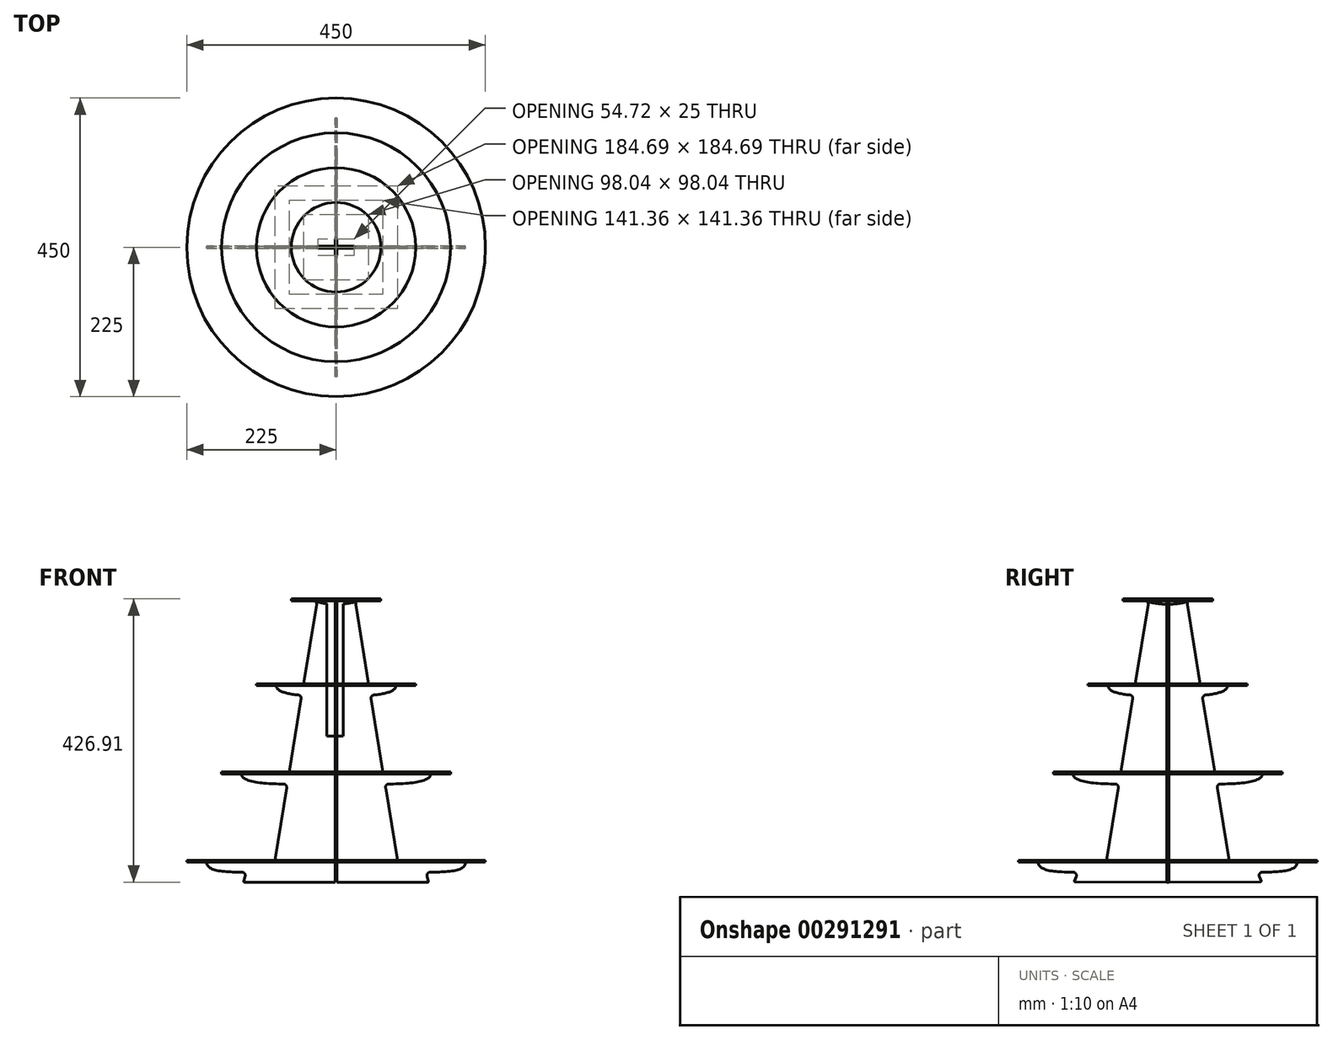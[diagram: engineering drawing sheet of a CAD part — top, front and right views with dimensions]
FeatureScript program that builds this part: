
annotation { "Feature Type Name" : "Feature", "Feature Type Description" : "" }
export const myFeature = defineFeature(function(context is Context, id is Id, definition is map)
    precondition{}
    {
        {
            var Q0;
            Q0=qCreatedBy(makeId("Front.planeOp"),FACE);
            var sketch = newSketch(context, id + "F0", { "sketchPlane" : qUnion([Q0])});
            skLineSegment(sketch, "E0.bottom", {"start": v(-225, 33) * mm, "end": v(225, 33) * mm, "construction": true});
            skLineSegment(sketch, "E0.top", {"start": v(-225, 30) * mm, "end": v(225, 30) * mm, "construction": true});
            skLineSegment(sketch, "E0.left", {"start": v(-225, 33) * mm, "end": v(-225, 30) * mm, "construction": true});
            skLineSegment(sketch, "E0.right", {"start": v(225, 33) * mm, "end": v(225, 30) * mm, "construction": true});
            skLineSegment(sketch, "E1.bottom", {"start": v(-172.5, 166) * mm, "end": v(172.5, 166) * mm, "construction": true});
            skLineSegment(sketch, "E1.top", {"start": v(-172.5, 163) * mm, "end": v(172.5, 163) * mm, "construction": true});
            skLineSegment(sketch, "E1.left", {"start": v(-172.5, 166) * mm, "end": v(-172.5, 163) * mm, "construction": true});
            skLineSegment(sketch, "E1.right", {"start": v(172.5, 166) * mm, "end": v(172.5, 163) * mm, "construction": true});
            skLineSegment(sketch, "E2.bottom", {"start": v(-120, 299) * mm, "end": v(120, 299) * mm, "construction": true});
            skLineSegment(sketch, "E2.top", {"start": v(-120, 296) * mm, "end": v(120, 296) * mm, "construction": true});
            skLineSegment(sketch, "E2.left", {"start": v(-120, 299) * mm, "end": v(-120, 296) * mm, "construction": true});
            skLineSegment(sketch, "E2.right", {"start": v(120, 299) * mm, "end": v(120, 296) * mm, "construction": true});
            skLineSegment(sketch, "E3.bottom", {"start": v(-67.5, 432) * mm, "end": v(67.5, 432) * mm, "construction": true});
            skLineSegment(sketch, "E3.top", {"start": v(-67.5, 429) * mm, "end": v(67.5, 429) * mm, "construction": true});
            skLineSegment(sketch, "E3.left", {"start": v(-67.5, 432) * mm, "end": v(-67.5, 429) * mm, "construction": true});
            skLineSegment(sketch, "E3.right", {"start": v(67.5, 432) * mm, "end": v(67.5, 429) * mm, "construction": true});
            skLineSegment(sketch, "E4", {"start": v(0, 0) * mm, "end": v(0, 600) * mm, "construction": true});
            skPoint(sketch, "E5", {"position": v(0, 30) * mm});
            skPoint(sketch, "E6", {"position": v(0, 163) * mm});
            skLineSegment(sketch, "E7", {"start": v(-225, 30) * mm, "end": v(0, 600) * mm, "construction": true});
            skPoint(sketch, "E8", {"position": v(0, 429) * mm});
            skPoint(sketch, "E9", {"position": v(0, 296) * mm});
            skFitSpline(sketch, "E10", {"points": [v(-195, 30) * mm, v(-135, 15) * mm], "startDerivative": vector(0, -45) * mm, "endDerivative": vector(85.44, 0) * mm});
            skFitSpline(sketch, "E11", {"points": [v(-142.5, 163) * mm, v(-82.5, 148) * mm], "startDerivative": vector(0, -35.84) * mm, "endDerivative": vector(85.44, 0) * mm});
            skLineSegment(sketch, "E12", {"start": v(-82.5, 148) * mm, "end": v(-79.5, 148) * mm});
            skFitSpline(sketch, "E13", {"points": [v(-90, 296) * mm, v(-30, 281) * mm], "startDerivative": vector(0, -35.84) * mm, "endDerivative": vector(85.44, 0) * mm});
            skLineSegment(sketch, "E14", {"start": v(-30, 281) * mm, "end": v(-3.68, 281) * mm});
            skFitSpline(sketch, "E15", {"points": [v(-37.5, 429) * mm, v(23.68, 417.72) * mm], "startDerivative": vector(0, -35.84) * mm, "endDerivative": vector(-10.64, 0) * mm});
            skLineSegment(sketch, "E16", {"start": v(-19.74, 478.8) * mm, "end": v(-27.36, 432) * mm});
            skLineSegment(sketch, "E17.trimOffspring", {"start": v(-74.56, 142.2) * mm, "end": v(-92.34, 33) * mm});
            skLineSegment(sketch, "E18.trimOffspring", {"start": v(-52.71, 276.35) * mm, "end": v(-70.68, 166) * mm});
            skLineSegment(sketch, "E19.trimOffspring", {"start": v(-29.56, 418.53) * mm, "end": v(-49.02, 299) * mm});
            skLineSegment(sketch, "E20", {"start": v(-92.34, 33) * mm, "end": v(-92.34, 30) * mm});
            skLineSegment(sketch, "E21", {"start": v(-92.34, 30) * mm, "end": v(-195, 30) * mm});
            skLineSegment(sketch, "E22", {"start": v(-70.68, 166) * mm, "end": v(-70.68, 163) * mm});
            skLineSegment(sketch, "E23", {"start": v(-70.68, 163) * mm, "end": v(-142.5, 163) * mm});
            skLineSegment(sketch, "E24", {"start": v(-49.02, 299) * mm, "end": v(-49.02, 296) * mm});
            skLineSegment(sketch, "E25", {"start": v(-49.02, 296) * mm, "end": v(-90, 296) * mm});
            skLineSegment(sketch, "E26", {"start": v(-27.36, 432) * mm, "end": v(-27.36, 429) * mm});
            skLineSegment(sketch, "E27", {"start": v(-27.36, 429) * mm, "end": v(-37.5, 429) * mm});
            skLineSegment(sketch, "E28", {"start": v(-137.04, 8.5) * mm, "end": v(-139.31, 1.3) * mm});
            skLineSegment(sketch, "E29", {"start": v(-138.36, 0) * mm, "end": v(0, 0) * mm});
            skArc(sketch, "E30.filletArc", {"start": v(-137.04, 8.5) * mm, "mid": v(-137.78, 12.96) * mm, "end": v(-141.8, 15) * mm});
            skPoint(sketch, "E31.visualSharp", {"position": v(-139.72, 0) * mm});
            skArc(sketch, "E31.filletArc", {"start": v(-139.31, 1.3) * mm, "mid": v(-139.16, 0.4) * mm, "end": v(-138.36, 0) * mm});
            skPoint(sketch, "E32.visualSharp", {"position": v(-73.61, 148) * mm});
            skArc(sketch, "E32.filletArc", {"start": v(-74.56, 142.2) * mm, "mid": v(-75.68, 146.24) * mm, "end": v(-79.5, 148) * mm});
            skPoint(sketch, "E33.visualSharp", {"position": v(-51.84, 281.7) * mm});
            skArc(sketch, "E33.filletArc", {"start": v(-52.71, 276.35) * mm, "mid": v(-53.69, 280.2) * mm, "end": v(-57.17, 282.13) * mm});
            skPoint(sketch, "E34.visualSharp", {"position": v(-28.89, 422.61) * mm});
            skArc(sketch, "E34.filletArc", {"start": v(-29.56, 418.53) * mm, "mid": v(-30.1, 421.72) * mm, "end": v(-32.48, 423.9) * mm});
            skLineSegment(sketch, "E35.MirrorCS", {"start": v(19.74, 478.8) * mm, "end": v(27.36, 432) * mm});
            skLineSegment(sketch, "E36.MirrorCS", {"start": v(27.36, 432) * mm, "end": v(27.36, 429) * mm});
            skLineSegment(sketch, "E37.MirrorCS", {"start": v(27.36, 429) * mm, "end": v(37.5, 429) * mm});
            skLineSegment(sketch, "E38.MirrorCS", {"start": v(67.5, 429) * mm, "end": v(-67.5, 429) * mm, "construction": true});
            skFitSpline(sketch, "E39.MirrorCS", {"points": [v(37.5, 429) * mm, v(-23.68, 417.72) * mm], "startDerivative": vector(0, -35.84) * mm, "endDerivative": vector(10.64, 0) * mm});
            skArc(sketch, "E40.MirrorCS", {"start": v(29.56, 418.53) * mm, "mid": v(30.1, 421.72) * mm, "end": v(32.48, 423.9) * mm});
            skLineSegment(sketch, "E41.MirrorCS", {"start": v(29.56, 418.53) * mm, "end": v(49.02, 299) * mm});
            skLineSegment(sketch, "E42.MirrorCS", {"start": v(49.02, 299) * mm, "end": v(49.02, 296) * mm});
            skLineSegment(sketch, "E43.MirrorCS", {"start": v(49.02, 296) * mm, "end": v(90, 296) * mm});
            skLineSegment(sketch, "E44.MirrorCS", {"start": v(120, 296) * mm, "end": v(-120, 296) * mm, "construction": true});
            skFitSpline(sketch, "E45.MirrorCS", {"points": [v(90, 296) * mm, v(30, 281) * mm], "startDerivative": vector(0, -35.84) * mm, "endDerivative": vector(-85.44, 0) * mm});
            skArc(sketch, "E46.MirrorCS", {"start": v(52.71, 276.35) * mm, "mid": v(53.69, 280.2) * mm, "end": v(57.17, 282.13) * mm});
            skLineSegment(sketch, "E47.MirrorCS", {"start": v(52.71, 276.35) * mm, "end": v(70.68, 166) * mm});
            skLineSegment(sketch, "E48.MirrorCS", {"start": v(70.68, 166) * mm, "end": v(70.68, 163) * mm});
            skLineSegment(sketch, "E49.MirrorCS", {"start": v(70.68, 163) * mm, "end": v(142.5, 163) * mm});
            skLineSegment(sketch, "E50.MirrorCS", {"start": v(172.5, 163) * mm, "end": v(-172.5, 163) * mm, "construction": true});
            skFitSpline(sketch, "E51.MirrorCS", {"points": [v(142.5, 163) * mm, v(82.5, 148) * mm], "startDerivative": vector(0, -35.84) * mm, "endDerivative": vector(-85.44, 0) * mm});
            skLineSegment(sketch, "E52.MirrorCS", {"start": v(74.56, 142.2) * mm, "end": v(92.34, 33) * mm});
            skLineSegment(sketch, "E53.MirrorCS", {"start": v(82.5, 148) * mm, "end": v(79.5, 148) * mm});
            skArc(sketch, "E54.MirrorCS", {"start": v(74.56, 142.2) * mm, "mid": v(75.68, 146.24) * mm, "end": v(79.5, 148) * mm});
            skPoint(sketch, "E55.MirrorP", {"position": v(73.61, 148) * mm});
            skLineSegment(sketch, "E56.MirrorCS", {"start": v(92.34, 30) * mm, "end": v(195, 30) * mm});
            skLineSegment(sketch, "E57.MirrorCS", {"start": v(225, 30) * mm, "end": v(-225, 30) * mm, "construction": true});
            skLineSegment(sketch, "E58.MirrorCS", {"start": v(92.34, 33) * mm, "end": v(92.34, 30) * mm});
            skFitSpline(sketch, "E59.MirrorCS", {"points": [v(195, 30) * mm, v(135, 15) * mm], "startDerivative": vector(0, -45) * mm, "endDerivative": vector(-85.44, 0) * mm});
            skArc(sketch, "E60.MirrorCS", {"start": v(137.04, 8.5) * mm, "mid": v(137.78, 12.96) * mm, "end": v(141.8, 15) * mm});
            skLineSegment(sketch, "E61.MirrorCS", {"start": v(137.04, 8.5) * mm, "end": v(139.31, 1.3) * mm});
            skArc(sketch, "E62.MirrorCS", {"start": v(139.31, 1.3) * mm, "mid": v(139.16, 0.4) * mm, "end": v(138.36, 0) * mm});
            skLineSegment(sketch, "E63.MirrorCS", {"start": v(138.36, 0) * mm, "end": v(0, 0) * mm});
            skPoint(sketch, "E64.visualSharp", {"position": v(0, 600) * mm});
            skPoint(sketch, "E65", {"position": v(0, 475.58) * mm});
            skArc(sketch, "E66.filletArc", {"start": v(19.74, 478.8) * mm, "mid": v(0, 495.58) * mm, "end": v(-19.74, 478.8) * mm});
            skCircle(sketch, "E67", {"center": v(0, 475.58) * mm, "radius": 10 * mm});
            skPoint(sketch, "E68", {"position": v(0, 495.58) * mm});
            skSolve(sketch);
        }
        {
            var Q0;
            Q0=makeQuery(id+"F0.imprint","IMPRINT",FACE,{"disambiguationData":[TD([[makeQuery(id+"F0.imprint","IMPRINT",EDGE,{"derivedFrom":sQuery(id+"F0.wireOp",EDGE,"E10")}),1.0]])]});
            extrude(context, id + "F1", {"entities" : qUnion([Q0]), "endBound" : BoundingType.SYMMETRIC, "depth" : 3 * mm});
        }
        {
            var Q0;
            Q0=makeQuery(id+"F1.opExtrude","CAP_FACE",FACE,{"disambiguationData":[OSD([sQuery(id+"F0.wireOp",EDGE,"E10"),sQuery(id+"F0.wireOp",EDGE,"E11"),sQuery(id+"F0.wireOp",EDGE,"E12"),sQuery(id+"F0.wireOp",EDGE,"E13"),sQuery(id+"F0.wireOp",EDGE,"E15"),sQuery(id+"F0.wireOp",EDGE,"E16"),sQuery(id+"F0.wireOp",EDGE,"E17.trimOffspring"),sQuery(id+"F0.wireOp",EDGE,"E18.trimOffspring"),sQuery(id+"F0.wireOp",EDGE,"E19.trimOffspring"),sQuery(id+"F0.wireOp",EDGE,"E20"),sQuery(id+"F0.wireOp",EDGE,"E21"),sQuery(id+"F0.wireOp",EDGE,"E22"),sQuery(id+"F0.wireOp",EDGE,"E23"),sQuery(id+"F0.wireOp",EDGE,"E24"),sQuery(id+"F0.wireOp",EDGE,"E25"),sQuery(id+"F0.wireOp",EDGE,"E26"),sQuery(id+"F0.wireOp",EDGE,"E27"),sQuery(id+"F0.wireOp",EDGE,"E28"),sQuery(id+"F0.wireOp",EDGE,"E29"),sQuery(id+"F0.wireOp",EDGE,"E30.filletArc"),sQuery(id+"F0.wireOp",EDGE,"E31.filletArc"),sQuery(id+"F0.wireOp",EDGE,"E32.filletArc"),sQuery(id+"F0.wireOp",EDGE,"E33.filletArc"),sQuery(id+"F0.wireOp",EDGE,"E34.filletArc"),sQuery(id+"F0.wireOp",EDGE,"E35.MirrorCS"),sQuery(id+"F0.wireOp",EDGE,"E36.MirrorCS"),sQuery(id+"F0.wireOp",EDGE,"E37.MirrorCS"),sQuery(id+"F0.wireOp",EDGE,"E39.MirrorCS"),sQuery(id+"F0.wireOp",EDGE,"E40.MirrorCS"),sQuery(id+"F0.wireOp",EDGE,"E41.MirrorCS"),sQuery(id+"F0.wireOp",EDGE,"E42.MirrorCS"),sQuery(id+"F0.wireOp",EDGE,"E43.MirrorCS"),sQuery(id+"F0.wireOp",EDGE,"E45.MirrorCS"),sQuery(id+"F0.wireOp",EDGE,"E46.MirrorCS"),sQuery(id+"F0.wireOp",EDGE,"E47.MirrorCS"),sQuery(id+"F0.wireOp",EDGE,"E48.MirrorCS"),sQuery(id+"F0.wireOp",EDGE,"E49.MirrorCS"),sQuery(id+"F0.wireOp",EDGE,"E51.MirrorCS"),sQuery(id+"F0.wireOp",EDGE,"E52.MirrorCS"),sQuery(id+"F0.wireOp",EDGE,"E53.MirrorCS"),sQuery(id+"F0.wireOp",EDGE,"E54.MirrorCS"),sQuery(id+"F0.wireOp",EDGE,"E56.MirrorCS"),sQuery(id+"F0.wireOp",EDGE,"E58.MirrorCS"),sQuery(id+"F0.wireOp",EDGE,"E59.MirrorCS"),sQuery(id+"F0.wireOp",EDGE,"E60.MirrorCS"),sQuery(id+"F0.wireOp",EDGE,"E61.MirrorCS"),sQuery(id+"F0.wireOp",EDGE,"E62.MirrorCS"),sQuery(id+"F0.wireOp",EDGE,"E63.MirrorCS"),sQuery(id+"F0.wireOp",EDGE,"E64.filletArc"),sQuery(id+"F0.wireOp",EDGE,"d411dd5c-ff6b-4678-903a-04fbd7847559.0"),sQuery(id+"F0.wireOp",EDGE,"kmb8QBBf-xoWS-FNvt-kf7i-W9jpLPe4fE8e"),sQuery(id+"F0.wireOp",EDGE,"0f97b2b1-3562-4e55-8034-25847450ba9d.filletArc"),sQuery(id+"F0.wireOp",EDGE,"a54b7074-a512-4e90-8ab1-eaa6c3fd8d95.filletArc")])],"isStart":false});
            var sketch = newSketch(context, id + "F2", { "sketchPlane" : qUnion([Q0])});
            skLineSegment(sketch, "E69.bottom", {"start": v(-1.5, 0) * mm, "end": v(1.5, 0) * mm});
            skLineSegment(sketch, "E69.top", {"start": v(-1.5, 220) * mm, "end": v(1.5, 220) * mm});
            skLineSegment(sketch, "E69.left", {"start": v(-1.5, 0) * mm, "end": v(-1.5, 220) * mm});
            skLineSegment(sketch, "E69.right", {"start": v(1.5, 0) * mm, "end": v(1.5, 220) * mm});
            skSolve(sketch);
        }
        {
            var Q0;
            Q0 = qSketchRegion(id + "F2", true);
            extrude(context, id + "F3", {"entities" : qUnion([Q0]), "operationType" : NewBodyOperationType.REMOVE, "oppositeDirection" : true, "depth" : 25 * mm});
        }
        {
            var Q0;
            Q0=qCreatedBy(makeId("Right.planeOp"),FACE);
            var sketch = newSketch(context, id + "F4", { "sketchPlane" : qUnion([Q0])});
            skLineSegment(sketch, "E70.bottom", {"start": v(-225, 33) * mm, "end": v(225, 33) * mm, "construction": true});
            skLineSegment(sketch, "E70.top", {"start": v(-225, 30) * mm, "end": v(225, 30) * mm, "construction": true});
            skLineSegment(sketch, "E70.left", {"start": v(-225, 33) * mm, "end": v(-225, 30) * mm, "construction": true});
            skLineSegment(sketch, "E70.right", {"start": v(225, 33) * mm, "end": v(225, 30) * mm, "construction": true});
            skLineSegment(sketch, "E71.bottom", {"start": v(-172.5, 166) * mm, "end": v(172.5, 166) * mm, "construction": true});
            skLineSegment(sketch, "E71.top", {"start": v(-172.5, 163) * mm, "end": v(172.5, 163) * mm, "construction": true});
            skLineSegment(sketch, "E71.left", {"start": v(-172.5, 166) * mm, "end": v(-172.5, 163) * mm, "construction": true});
            skLineSegment(sketch, "E71.right", {"start": v(172.5, 166) * mm, "end": v(172.5, 163) * mm, "construction": true});
            skLineSegment(sketch, "E72.bottom", {"start": v(-120, 299) * mm, "end": v(120, 299) * mm, "construction": true});
            skLineSegment(sketch, "E72.top", {"start": v(-120, 296) * mm, "end": v(120, 296) * mm, "construction": true});
            skLineSegment(sketch, "E72.left", {"start": v(-120, 299) * mm, "end": v(-120, 296) * mm, "construction": true});
            skLineSegment(sketch, "E72.right", {"start": v(120, 299) * mm, "end": v(120, 296) * mm, "construction": true});
            skLineSegment(sketch, "E73.bottom", {"start": v(-67.5, 432) * mm, "end": v(67.5, 432) * mm, "construction": true});
            skLineSegment(sketch, "E73.top", {"start": v(-67.5, 429) * mm, "end": v(67.5, 429) * mm, "construction": true});
            skLineSegment(sketch, "E73.left", {"start": v(-67.5, 432) * mm, "end": v(-67.5, 429) * mm, "construction": true});
            skLineSegment(sketch, "E73.right", {"start": v(67.5, 432) * mm, "end": v(67.5, 429) * mm, "construction": true});
            skLineSegment(sketch, "E74", {"start": v(0, 0) * mm, "end": v(0, 600) * mm, "construction": true});
            skPoint(sketch, "E75", {"position": v(0, 30) * mm});
            skPoint(sketch, "E76", {"position": v(0, 163) * mm});
            skLineSegment(sketch, "E77", {"start": v(-225, 30) * mm, "end": v(0, 600) * mm, "construction": true});
            skPoint(sketch, "E78", {"position": v(0, 429) * mm});
            skPoint(sketch, "E79", {"position": v(0, 296) * mm});
            skFitSpline(sketch, "E80", {"points": [v(-195, 30) * mm, v(-135, 15) * mm], "startDerivative": vector(0, -45) * mm, "endDerivative": vector(84.25, 0) * mm});
            skFitSpline(sketch, "E81", {"points": [v(-142.5, 163) * mm, v(-82.5, 148) * mm], "startDerivative": vector(0, -35.84) * mm, "endDerivative": vector(85.44, 0) * mm});
            skLineSegment(sketch, "E82", {"start": v(-82.5, 148) * mm, "end": v(-79.5, 148) * mm});
            skFitSpline(sketch, "E83", {"points": [v(-90, 296) * mm, v(-30, 281) * mm], "startDerivative": vector(0, -35.84) * mm, "endDerivative": vector(85.44, 0) * mm});
            skLineSegment(sketch, "E84", {"start": v(-30, 281) * mm, "end": v(-3.68, 281) * mm});
            skFitSpline(sketch, "E85", {"points": [v(-37.5, 429) * mm, v(23.68, 417.72) * mm], "startDerivative": vector(0, -35.84) * mm, "endDerivative": vector(-10.64, 0) * mm});
            skLineSegment(sketch, "E86.trimOffspring", {"start": v(-74.56, 142.2) * mm, "end": v(-92.34, 33) * mm});
            skLineSegment(sketch, "E87.trimOffspring", {"start": v(-52.71, 276.35) * mm, "end": v(-70.68, 166) * mm});
            skLineSegment(sketch, "E88.trimOffspring", {"start": v(-29.56, 418.53) * mm, "end": v(-49.02, 299) * mm});
            skLineSegment(sketch, "E89", {"start": v(-92.34, 33) * mm, "end": v(-92.34, 30) * mm});
            skLineSegment(sketch, "E90", {"start": v(-92.34, 30) * mm, "end": v(-195, 30) * mm});
            skLineSegment(sketch, "E91", {"start": v(-70.68, 166) * mm, "end": v(-70.68, 163) * mm});
            skLineSegment(sketch, "E92", {"start": v(-70.68, 163) * mm, "end": v(-142.5, 163) * mm});
            skLineSegment(sketch, "E93", {"start": v(-49.02, 299) * mm, "end": v(-49.02, 296) * mm});
            skLineSegment(sketch, "E94", {"start": v(-49.02, 296) * mm, "end": v(-90, 296) * mm});
            skLineSegment(sketch, "E95", {"start": v(-12.5, 432) * mm, "end": v(-12.5, 429) * mm});
            skLineSegment(sketch, "E96", {"start": v(-12.5, 429) * mm, "end": v(-37.5, 429) * mm});
            skLineSegment(sketch, "E97", {"start": v(-138, 8.04) * mm, "end": v(-140.63, 1.9) * mm});
            skLineSegment(sketch, "E98", {"start": v(-139.72, 0.5) * mm, "end": v(0, 0) * mm});
            skArc(sketch, "E99.filletArc", {"start": v(-138, 8.04) * mm, "mid": v(-138.4, 12.75) * mm, "end": v(-142.56, 15.01) * mm});
            skPoint(sketch, "E100.visualSharp", {"position": v(-141.23, 0.5) * mm});
            skArc(sketch, "E100.filletArc", {"start": v(-140.63, 1.9) * mm, "mid": v(-140.55, 0.95) * mm, "end": v(-139.72, 0.5) * mm});
            skPoint(sketch, "E101.visualSharp", {"position": v(-73.61, 148) * mm});
            skArc(sketch, "E101.filletArc", {"start": v(-74.56, 142.2) * mm, "mid": v(-75.68, 146.24) * mm, "end": v(-79.5, 148) * mm});
            skPoint(sketch, "E102.visualSharp", {"position": v(-51.84, 281.7) * mm});
            skArc(sketch, "E102.filletArc", {"start": v(-52.71, 276.35) * mm, "mid": v(-53.69, 280.2) * mm, "end": v(-57.17, 282.13) * mm});
            skPoint(sketch, "E103.visualSharp", {"position": v(-28.89, 422.61) * mm});
            skArc(sketch, "E103.filletArc", {"start": v(-29.56, 418.53) * mm, "mid": v(-30.1, 421.72) * mm, "end": v(-32.48, 423.9) * mm});
            skLineSegment(sketch, "E104.MirrorCS", {"start": v(12.5, 432) * mm, "end": v(12.5, 429) * mm});
            skLineSegment(sketch, "E105.MirrorCS", {"start": v(12.5, 429) * mm, "end": v(37.5, 429) * mm});
            skLineSegment(sketch, "E106.MirrorCS", {"start": v(67.5, 429) * mm, "end": v(-67.5, 429) * mm, "construction": true});
            skFitSpline(sketch, "E107.MirrorCS", {"points": [v(37.5, 429) * mm, v(-23.68, 417.72) * mm], "startDerivative": vector(0, -35.84) * mm, "endDerivative": vector(10.64, 0) * mm});
            skArc(sketch, "E108.MirrorCS", {"start": v(29.56, 418.53) * mm, "mid": v(30.1, 421.72) * mm, "end": v(32.48, 423.9) * mm});
            skLineSegment(sketch, "E109.MirrorCS", {"start": v(29.56, 418.53) * mm, "end": v(49.02, 299) * mm});
            skLineSegment(sketch, "E110.MirrorCS", {"start": v(49.02, 299) * mm, "end": v(49.02, 296) * mm});
            skLineSegment(sketch, "E111.MirrorCS", {"start": v(49.02, 296) * mm, "end": v(90, 296) * mm});
            skLineSegment(sketch, "E112.MirrorCS", {"start": v(120, 296) * mm, "end": v(-120, 296) * mm, "construction": true});
            skFitSpline(sketch, "E113.MirrorCS", {"points": [v(90, 296) * mm, v(30, 281) * mm], "startDerivative": vector(0, -35.84) * mm, "endDerivative": vector(-85.44, 0) * mm});
            skArc(sketch, "E114.MirrorCS", {"start": v(52.71, 276.35) * mm, "mid": v(53.69, 280.2) * mm, "end": v(57.17, 282.13) * mm});
            skLineSegment(sketch, "E115.MirrorCS", {"start": v(52.71, 276.35) * mm, "end": v(70.68, 166) * mm});
            skLineSegment(sketch, "E116.MirrorCS", {"start": v(70.68, 166) * mm, "end": v(70.68, 163) * mm});
            skLineSegment(sketch, "E117.MirrorCS", {"start": v(70.68, 163) * mm, "end": v(142.5, 163) * mm});
            skLineSegment(sketch, "E118.MirrorCS", {"start": v(172.5, 163) * mm, "end": v(-172.5, 163) * mm, "construction": true});
            skFitSpline(sketch, "E119.MirrorCS", {"points": [v(142.5, 163) * mm, v(82.5, 148) * mm], "startDerivative": vector(0, -35.84) * mm, "endDerivative": vector(-85.44, 0) * mm});
            skLineSegment(sketch, "E120.MirrorCS", {"start": v(74.56, 142.2) * mm, "end": v(92.34, 33) * mm});
            skLineSegment(sketch, "E121.MirrorCS", {"start": v(82.5, 148) * mm, "end": v(79.5, 148) * mm});
            skArc(sketch, "E122.MirrorCS", {"start": v(74.56, 142.2) * mm, "mid": v(75.68, 146.24) * mm, "end": v(79.5, 148) * mm});
            skPoint(sketch, "E123.MirrorP", {"position": v(73.61, 148) * mm});
            skLineSegment(sketch, "E124.MirrorCS", {"start": v(92.34, 30) * mm, "end": v(195, 30) * mm});
            skLineSegment(sketch, "E125.MirrorCS", {"start": v(225, 30) * mm, "end": v(-225, 30) * mm, "construction": true});
            skLineSegment(sketch, "E126.MirrorCS", {"start": v(92.34, 33) * mm, "end": v(92.34, 30) * mm});
            skFitSpline(sketch, "E127.MirrorCS", {"points": [v(195, 30) * mm, v(135, 15) * mm], "startDerivative": vector(0, -45) * mm, "endDerivative": vector(-84.25, 0) * mm});
            skArc(sketch, "E128.MirrorCS", {"start": v(138, 8.04) * mm, "mid": v(138.4, 12.75) * mm, "end": v(142.56, 15.01) * mm});
            skLineSegment(sketch, "E129.MirrorCS", {"start": v(138, 8.04) * mm, "end": v(140.63, 1.9) * mm});
            skArc(sketch, "E130.MirrorCS", {"start": v(140.63, 1.9) * mm, "mid": v(140.55, 0.95) * mm, "end": v(139.72, 0.5) * mm});
            skLineSegment(sketch, "E131.MirrorCS", {"start": v(139.72, 0.5) * mm, "end": v(0, 0) * mm});
            skPoint(sketch, "E132.visualSharp", {"position": v(0, 600) * mm});
            skPoint(sketch, "E133", {"position": v(0, 495.58) * mm});
            skLineSegment(sketch, "E134", {"start": v(-12.5, 432) * mm, "end": v(12.5, 432) * mm});
            skSolve(sketch);
        }
        {
            var Q0;
            Q0=makeQuery(id+"F4.imprint","IMPRINT",FACE,{"disambiguationData":[TD([[makeQuery(id+"F4.imprint","IMPRINT",EDGE,{"derivedFrom":sQuery(id+"F4.wireOp",EDGE,"E80")}),1.0]])]});
            extrude(context, id + "F5", {"entities" : qUnion([Q0]), "endBound" : BoundingType.SYMMETRIC, "depth" : 3 * mm});
        }
        {
            var Q0;
            Q0=makeQuery(id+"F5.opExtrude","CAP_FACE",FACE,{"disambiguationData":[OSD([sQuery(id+"F4.wireOp",EDGE,"E80"),sQuery(id+"F4.wireOp",EDGE,"E81"),sQuery(id+"F4.wireOp",EDGE,"E82"),sQuery(id+"F4.wireOp",EDGE,"E83"),sQuery(id+"F4.wireOp",EDGE,"E85"),sQuery(id+"F4.wireOp",EDGE,"E86.trimOffspring"),sQuery(id+"F4.wireOp",EDGE,"E87.trimOffspring"),sQuery(id+"F4.wireOp",EDGE,"E88.trimOffspring"),sQuery(id+"F4.wireOp",EDGE,"E89"),sQuery(id+"F4.wireOp",EDGE,"E90"),sQuery(id+"F4.wireOp",EDGE,"E91"),sQuery(id+"F4.wireOp",EDGE,"E92"),sQuery(id+"F4.wireOp",EDGE,"E93"),sQuery(id+"F4.wireOp",EDGE,"E94"),sQuery(id+"F4.wireOp",EDGE,"E95"),sQuery(id+"F4.wireOp",EDGE,"E96"),sQuery(id+"F4.wireOp",EDGE,"E97"),sQuery(id+"F4.wireOp",EDGE,"E98"),sQuery(id+"F4.wireOp",EDGE,"E99.filletArc"),sQuery(id+"F4.wireOp",EDGE,"E100.filletArc"),sQuery(id+"F4.wireOp",EDGE,"E101.filletArc"),sQuery(id+"F4.wireOp",EDGE,"E102.filletArc"),sQuery(id+"F4.wireOp",EDGE,"E103.filletArc"),sQuery(id+"F4.wireOp",EDGE,"E104.MirrorCS"),sQuery(id+"F4.wireOp",EDGE,"E105.MirrorCS"),sQuery(id+"F4.wireOp",EDGE,"E107.MirrorCS"),sQuery(id+"F4.wireOp",EDGE,"E108.MirrorCS"),sQuery(id+"F4.wireOp",EDGE,"E109.MirrorCS"),sQuery(id+"F4.wireOp",EDGE,"E110.MirrorCS"),sQuery(id+"F4.wireOp",EDGE,"E111.MirrorCS"),sQuery(id+"F4.wireOp",EDGE,"E113.MirrorCS"),sQuery(id+"F4.wireOp",EDGE,"E114.MirrorCS"),sQuery(id+"F4.wireOp",EDGE,"E115.MirrorCS"),sQuery(id+"F4.wireOp",EDGE,"E116.MirrorCS"),sQuery(id+"F4.wireOp",EDGE,"E117.MirrorCS"),sQuery(id+"F4.wireOp",EDGE,"E119.MirrorCS"),sQuery(id+"F4.wireOp",EDGE,"E120.MirrorCS"),sQuery(id+"F4.wireOp",EDGE,"E121.MirrorCS"),sQuery(id+"F4.wireOp",EDGE,"E122.MirrorCS"),sQuery(id+"F4.wireOp",EDGE,"E124.MirrorCS"),sQuery(id+"F4.wireOp",EDGE,"E126.MirrorCS"),sQuery(id+"F4.wireOp",EDGE,"E127.MirrorCS"),sQuery(id+"F4.wireOp",EDGE,"E128.MirrorCS"),sQuery(id+"F4.wireOp",EDGE,"E129.MirrorCS"),sQuery(id+"F4.wireOp",EDGE,"E130.MirrorCS"),sQuery(id+"F4.wireOp",EDGE,"E131.MirrorCS"),sQuery(id+"F4.wireOp",EDGE,"E134")])],"isStart":true});
            var sketch = newSketch(context, id + "F6", { "sketchPlane" : qUnion([Q0])});
            skLineSegment(sketch, "E135.bottom", {"start": v(-1.5, 432) * mm, "end": v(1.5, 432) * mm});
            skLineSegment(sketch, "E135.top", {"start": v(-1.5, 220) * mm, "end": v(1.5, 220) * mm});
            skLineSegment(sketch, "E135.left", {"start": v(-1.5, 432) * mm, "end": v(-1.5, 220) * mm});
            skLineSegment(sketch, "E135.right", {"start": v(1.5, 432) * mm, "end": v(1.5, 220) * mm});
            skSolve(sketch);
        }
        {
            var Q0;
            Q0 = qSketchRegion(id + "F6", true);
            extrude(context, id + "F7", {"entities" : qUnion([Q0]), "operationType" : NewBodyOperationType.REMOVE, "endBound" : BoundingType.SYMMETRIC, "oppositeDirection" : true, "depth" : 25 * mm});
        }
        {
            var Q0;
            Q0=qCreatedBy(makeId("Top.planeOp"),FACE);
            var Q1;
            Q1=makeQuery(id+"F1.opExtrude","CAP_VERTEX",VERTEX,{"disambiguationData":[OSD([sQuery(id+"F0.wireOp",EDGE,"E10"),sQuery(id+"F0.wireOp",EDGE,"E21")])],"isStart":false});
            cPlane(context, id + "F8", {"entities" : qUnion([Q0, Q1]), "cplaneType" : CPlaneType.PLANE_POINT, "offset" : 25 * mm, "width" : 150 * mm, "height" : 150 * mm});
        }
        {
            var Q0;
            Q0=qCreatedBy(id+"F8.planeOp",FACE);
            var sketch = newSketch(context, id + "F9", { "sketchPlane" : qUnion([Q0])});
            skPoint(sketch, "E136.0", {"position": v(0, 0) * mm});
            skLineSegment(sketch, "E137.0", {"start": v(-92.34, -1.5) * mm, "end": v(-92.34, 1.5) * mm});
            skLineSegment(sketch, "E138.0", {"start": v(1.5, -92.34) * mm, "end": v(-1.5, -92.34) * mm});
            skLineSegment(sketch, "E139.0", {"start": v(92.34, -1.5) * mm, "end": v(92.34, 1.5) * mm});
            skLineSegment(sketch, "E140.0", {"start": v(1.5, 92.34) * mm, "end": v(-1.5, 92.34) * mm});
            skLineSegment(sketch, "E141.0", {"start": v(-225, 0) * mm, "end": v(225, 0) * mm, "construction": true});
            skCircle(sketch, "E142", {"center": v(0, 0) * mm, "radius": 225 * mm});
            skLineSegment(sketch, "E143", {"start": v(-1.5, 92.34) * mm, "end": v(-1.5, 1.5) * mm});
            skLineSegment(sketch, "E144", {"start": v(1.5, -92.34) * mm, "end": v(1.5, -1.5) * mm});
            skLineSegment(sketch, "E145", {"start": v(92.34, 1.5) * mm, "end": v(1.5, 1.5) * mm});
            skLineSegment(sketch, "E146", {"start": v(-92.34, -1.5) * mm, "end": v(-1.5, -1.5) * mm});
            skLineSegment(sketch, "E147.trimOffspring", {"start": v(-1.5, 1.5) * mm, "end": v(-92.34, 1.5) * mm});
            skLineSegment(sketch, "E148.trimOffspring", {"start": v(1.5, 1.5) * mm, "end": v(1.5, 92.34) * mm});
            skLineSegment(sketch, "E149.trimOffspring", {"start": v(1.5, -1.5) * mm, "end": v(92.34, -1.5) * mm});
            skLineSegment(sketch, "E150.trimOffspring", {"start": v(-1.5, -1.5) * mm, "end": v(-1.5, -92.34) * mm});
            skSolve(sketch);
        }
        {
            var Q0;
            Q0=makeQuery(id+"F9.imprint","IMPRINT",FACE,{"disambiguationData":[TD([[makeQuery(id+"F9.imprint","IMPRINT",EDGE,{"derivedFrom":sQuery(id+"F9.wireOp",EDGE,"E137.0")}),1.0]])]});
            extrude(context, id + "F10", {"entities" : qUnion([Q0]), "depth" : 3 * mm});
        }
        {
            var Q0;
            Q0=qCreatedBy(makeId("Top.planeOp"),FACE);
            var Q1;
            Q1=makeQuery(id+"F5.opExtrude","CAP_VERTEX",VERTEX,{"disambiguationData":[OSD([sQuery(id+"F4.wireOp",EDGE,"E81"),sQuery(id+"F4.wireOp",EDGE,"E92")])],"isStart":false});
            cPlane(context, id + "F11", {"entities" : qUnion([Q0, Q1]), "cplaneType" : CPlaneType.PLANE_POINT, "offset" : 25 * mm, "width" : 150 * mm, "height" : 150 * mm});
        }
        {
            var Q0;
            Q0=qCreatedBy(id+"F11.planeOp",FACE);
            var sketch = newSketch(context, id + "F12", { "sketchPlane" : qUnion([Q0])});
            skPoint(sketch, "E151.0", {"position": v(0, 0) * mm});
            skLineSegment(sketch, "E152.0", {"start": v(1.5, -70.68) * mm, "end": v(-1.5, -70.68) * mm});
            skLineSegment(sketch, "E153.0", {"start": v(70.68, -1.5) * mm, "end": v(70.68, 1.5) * mm});
            skLineSegment(sketch, "E154.0", {"start": v(1.5, 70.68) * mm, "end": v(-1.5, 70.68) * mm});
            skLineSegment(sketch, "E155.0", {"start": v(-70.68, -1.5) * mm, "end": v(-70.68, 1.5) * mm});
            skLineSegment(sketch, "E156.0", {"start": v(-172.5, 0) * mm, "end": v(172.5, 0) * mm, "construction": true});
            skCircle(sketch, "E157", {"center": v(0, 0) * mm, "radius": 172.5 * mm});
            skLineSegment(sketch, "E158", {"start": v(-70.68, 1.5) * mm, "end": v(-1.5, 1.5) * mm});
            skLineSegment(sketch, "E159", {"start": v(70.68, -1.5) * mm, "end": v(1.5, -1.5) * mm});
            skLineSegment(sketch, "E160", {"start": v(-1.5, -70.68) * mm, "end": v(-1.5, -1.5) * mm});
            skLineSegment(sketch, "E161", {"start": v(1.5, 70.68) * mm, "end": v(1.5, 1.5) * mm});
            skLineSegment(sketch, "E162.trimOffspring", {"start": v(-1.5, -1.5) * mm, "end": v(-70.68, -1.5) * mm});
            skLineSegment(sketch, "E163.trimOffspring", {"start": v(-1.5, 1.5) * mm, "end": v(-1.5, 70.68) * mm});
            skLineSegment(sketch, "E164.trimOffspring", {"start": v(1.5, 1.5) * mm, "end": v(70.68, 1.5) * mm});
            skLineSegment(sketch, "E165.trimOffspring", {"start": v(1.5, -1.5) * mm, "end": v(1.5, -70.68) * mm});
            skSolve(sketch);
        }
        {
            var Q0;
            Q0=makeQuery(id+"F12.imprint","IMPRINT",FACE,{"disambiguationData":[TD([[makeQuery(id+"F12.imprint","IMPRINT",EDGE,{"derivedFrom":sQuery(id+"F12.wireOp",EDGE,"E152.0")}),1.0]])]});
            extrude(context, id + "F13", {"entities" : qUnion([Q0]), "depth" : 3 * mm});
        }
        {
            var Q0;
            Q0=qCreatedBy(makeId("Top.planeOp"),FACE);
            var Q1;
            Q1=makeQuery(id+"F5.opExtrude","CAP_VERTEX",VERTEX,{"disambiguationData":[OSD([sQuery(id+"F4.wireOp",EDGE,"E83"),sQuery(id+"F4.wireOp",EDGE,"E94")])],"isStart":false});
            cPlane(context, id + "F14", {"entities" : qUnion([Q0, Q1]), "cplaneType" : CPlaneType.PLANE_POINT, "offset" : 25 * mm, "width" : 150 * mm, "height" : 150 * mm});
        }
        {
            var Q0;
            Q0=qCreatedBy(id+"F14.planeOp",FACE);
            var sketch = newSketch(context, id + "F15", { "sketchPlane" : qUnion([Q0])});
            skPoint(sketch, "E166.0", {"position": v(0, 0) * mm});
            skPoint(sketch, "E167.0", {"position": v(0, -49.02) * mm});
            skLineSegment(sketch, "E168.0", {"start": v(1.5, -49.02) * mm, "end": v(-1.5, -49.02) * mm});
            skLineSegment(sketch, "E169.0", {"start": v(49.02, -1.5) * mm, "end": v(49.02, 1.5) * mm});
            skLineSegment(sketch, "E170.0", {"start": v(1.5, 49.02) * mm, "end": v(-1.5, 49.02) * mm});
            skLineSegment(sketch, "E171.0", {"start": v(-49.02, -1.5) * mm, "end": v(-49.02, 1.5) * mm});
            skLineSegment(sketch, "E172.0", {"start": v(-120, 0) * mm, "end": v(120, 0) * mm, "construction": true});
            skCircle(sketch, "E173", {"center": v(0, 0) * mm, "radius": 120 * mm});
            skLineSegment(sketch, "E174", {"start": v(-1.5, -49.02) * mm, "end": v(-1.5, -1.5) * mm});
            skLineSegment(sketch, "E175", {"start": v(49.02, -1.5) * mm, "end": v(1.5, -1.5) * mm});
            skLineSegment(sketch, "E176", {"start": v(-49.02, 1.5) * mm, "end": v(-1.5, 1.5) * mm});
            skLineSegment(sketch, "E177.trimOffspring", {"start": v(1.5, 1.5) * mm, "end": v(49.02, 1.5) * mm});
            skLineSegment(sketch, "E178.trimOffspring", {"start": v(1.5, -1.5) * mm, "end": v(1.5, -49.02) * mm});
            skLineSegment(sketch, "E179.trimOffspring", {"start": v(-1.5, -1.5) * mm, "end": v(-49.02, -1.5) * mm});
            skLineSegment(sketch, "E180.trimOffspring", {"start": v(-1.5, 1.5) * mm, "end": v(-1.5, 49.02) * mm});
            skLineSegment(sketch, "E181", {"start": v(1.5, 1.5) * mm, "end": v(1.5, 49.02) * mm});
            skSolve(sketch);
        }
        {
            var Q0;
            Q0=makeQuery(id+"F15.imprint","IMPRINT",FACE,{"disambiguationData":[TD([[makeQuery(id+"F15.imprint","IMPRINT",EDGE,{"derivedFrom":sQuery(id+"F15.wireOp",EDGE,"E168.0")}),1.0]])]});
            extrude(context, id + "F16", {"entities" : qUnion([Q0]), "depth" : 3 * mm});
        }
        {
            var Q0;
            Q0=qCreatedBy(makeId("Top.planeOp"),FACE);
            var Q1;
            Q1=makeQuery(id+"F1.opExtrude","CAP_VERTEX",VERTEX,{"disambiguationData":[OSD([sQuery(id+"F0.wireOp",EDGE,"E15"),sQuery(id+"F0.wireOp",EDGE,"E27")])],"isStart":false});
            cPlane(context, id + "F17", {"entities" : qUnion([Q0, Q1]), "cplaneType" : CPlaneType.PLANE_POINT, "offset" : 25 * mm, "width" : 150 * mm, "height" : 150 * mm});
        }
        {
            var Q0;
            Q0=qCreatedBy(id+"F17.planeOp",FACE);
            var sketch = newSketch(context, id + "F18", { "sketchPlane" : qUnion([Q0])});
            skLineSegment(sketch, "E182.0", {"start": v(-27.36, -1.5) * mm, "end": v(-27.36, 1.5) * mm});
            skLineSegment(sketch, "E183.0", {"start": v(1.5, -12.5) * mm, "end": v(-1.5, -12.5) * mm});
            skLineSegment(sketch, "E184.0", {"start": v(27.36, -1.5) * mm, "end": v(27.36, 1.5) * mm});
            skLineSegment(sketch, "E185.0", {"start": v(1.5, 12.5) * mm, "end": v(-1.5, 12.5) * mm});
            skLineSegment(sketch, "E186.0", {"start": v(-67.5, 0) * mm, "end": v(67.5, 0) * mm, "construction": true});
            skPoint(sketch, "E187.0", {"position": v(0, 0) * mm});
            skCircle(sketch, "E188", {"center": v(0, 0) * mm, "radius": 67.5 * mm});
            skLineSegment(sketch, "E189", {"start": v(-1.5, 12.5) * mm, "end": v(-1.5, 1.5) * mm});
            skLineSegment(sketch, "E190", {"start": v(1.5, 12.5) * mm, "end": v(1.5, 1.5) * mm});
            skLineSegment(sketch, "E191", {"start": v(27.36, -1.5) * mm, "end": v(1.5, -1.5) * mm});
            skLineSegment(sketch, "E192", {"start": v(-27.36, 1.5) * mm, "end": v(-1.5, 1.5) * mm});
            skLineSegment(sketch, "E193.trimOffspring", {"start": v(-1.5, -1.5) * mm, "end": v(-27.36, -1.5) * mm});
            skLineSegment(sketch, "E194.trimOffspring", {"start": v(-1.5, -1.5) * mm, "end": v(-1.5, -12.5) * mm});
            skLineSegment(sketch, "E195.trimOffspring", {"start": v(1.5, 1.5) * mm, "end": v(27.36, 1.5) * mm});
            skLineSegment(sketch, "E196.trimOffspring", {"start": v(1.5, -1.5) * mm, "end": v(1.5, -12.5) * mm});
            skSolve(sketch);
        }
        {
            var Q0;
            Q0=makeQuery(id+"F18.imprint","IMPRINT",FACE,{"disambiguationData":[TD([[makeQuery(id+"F18.imprint","IMPRINT",EDGE,{"derivedFrom":sQuery(id+"F18.wireOp",EDGE,"E182.0")}),1.0]])]});
            extrude(context, id + "F19", {"entities" : qUnion([Q0]), "depth" : 3 * mm});
        }
    });
